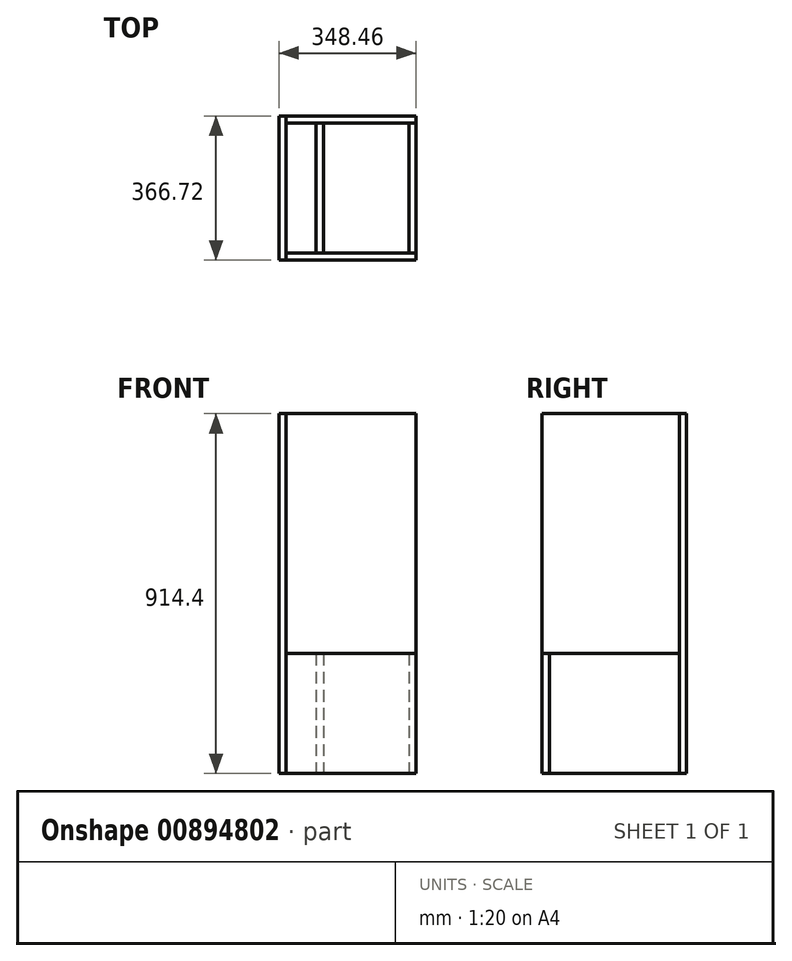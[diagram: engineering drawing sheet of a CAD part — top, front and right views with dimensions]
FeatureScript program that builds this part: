
annotation { "Feature Type Name" : "Feature", "Feature Type Description" : "" }
export const myFeature = defineFeature(function(context is Context, id is Id, definition is map)
    precondition{}
    {
        {
            assignVariable(context, id + "F0", {"name" : "PlyThick", "anyValue" : 23 / 812.8 * mm});
        }
        {
            assignVariable(context, id + "F1", {"name" : "HeightBack", "anyValue" : 914.4 * mm});
        }
        {
            assignVariable(context, id + "F2", {"name" : "HeightFront", "anyValue" : 304.8 * mm});
        }
        {
            var Q0;
            Q0=qCreatedBy(makeId("Top.planeOp"),FACE);
            var sketch = newSketch(context, id + "F3", { "sketchPlane" : qUnion([Q0])});
            skLineSegment(sketch, "E0.bottom", {"start": v(174.23, -183.36) * mm, "end": v(-174.23, -183.36) * mm});
            skLineSegment(sketch, "E0.top", {"start": v(174.23, 183.36) * mm, "end": v(-174.23, 183.36) * mm});
            skLineSegment(sketch, "E0.left", {"start": v(174.23, -183.36) * mm, "end": v(174.23, 183.36) * mm});
            skLineSegment(sketch, "E0.right", {"start": v(-174.23, -183.36) * mm, "end": v(-174.23, 183.36) * mm});
            skPoint(sketch, "E0.middle", {"position": v(0, 0) * mm});
            skLineSegment(sketch, "E1", {"start": v(-155.97, -183.36) * mm, "end": v(-155.97, 183.36) * mm});
            skLineSegment(sketch, "E2", {"start": v(-155.97, 165.1) * mm, "end": v(174.23, 165.1) * mm});
            skLineSegment(sketch, "E3", {"start": v(155.97, 165.1) * mm, "end": v(155.97, -165.1) * mm});
            skLineSegment(sketch, "E4", {"start": v(174.23, -165.1) * mm, "end": v(-155.97, -165.1) * mm});
            skLineSegment(sketch, "E5", {"start": v(-79.77, 165.1) * mm, "end": v(-79.77, -165.1) * mm, "construction": true});
            skLineSegment(sketch, "E6", {"start": v(-61.52, -165.1) * mm, "end": v(-61.52, 165.1) * mm, "construction": true});
            skSolve(sketch);
        }
        {
            var Q0;
            Q0=qCreatedBy(makeId("Top.planeOp"),FACE);
            var sketch = newSketch(context, id + "F4", { "sketchPlane" : qUnion([Q0])});
            skLineSegment(sketch, "E7.0.0", {"start": v(-155.97, -165.1) * mm, "end": v(155.97, -165.1) * mm});
            skLineSegment(sketch, "E7.0.1", {"start": v(155.97, -165.1) * mm, "end": v(155.97, 165.1) * mm});
            skLineSegment(sketch, "E7.0.2", {"start": v(155.97, 165.1) * mm, "end": v(-155.97, 165.1) * mm});
            skLineSegment(sketch, "E7.0.3", {"start": v(-155.97, 165.1) * mm, "end": v(-155.97, -165.1) * mm});
            skSolve(sketch);
        }
        {
            var Q0;
            Q0 = qSketchRegion(id + "F4", true);
            extrude(context, id + "F5", {"entities" : qUnion([Q0]), "depth" : getVariable(context, 'PlyThick'), "offsetDistance" : 25.4 * mm});
        }
        {
            var Q0;
            {var subQ4=sQuery(id+"F3.wireOp",EDGE,"E0.right");Q0=makeQuery(id+"F3.imprint","IMPRINT",FACE,{"disambiguationData":[TD([[makeQuery(id+"F3.imprint","IMPRINT",EDGE,{"derivedFrom":subQ4}),-1.0]])]});}
            extrude(context, id + "F6", {"entities" : qUnion([Q0]), "depth" : getVariable(context, 'HeightBack'), "offsetDistance" : 25.4 * mm});
        }
        {
            var Q0;
            {var subQ1=sQuery(id+"F3.wireOp",EDGE,"E0.top");var subQ6=sQuery(id+"F3.wireOp",EDGE,"E0.left");var subQ7=makeQuery(id+"F3.imprint","INTERSECT",VERTEX,{"derivedFrom":[subQ1,subQ6]});Q0=makeQuery(id+"F3.imprint","IMPRINT",FACE,{"disambiguationData":[TD([[makeQuery(id+"F3.imprint","IMPRINT",EDGE,{"disambiguationData":[TD([[subQ7,-1.0]])],"derivedFrom":subQ1}),1.0]])]});}
            extrude(context, id + "F7", {"entities" : qUnion([Q0]), "depth" : getVariable(context, 'HeightBack'), "offsetDistance" : 25.4 * mm});
        }
        {
            var Q0;
            {var subQ5=sQuery(id+"F3.wireOp",EDGE,"E4");Q0=makeQuery(id+"F3.imprint","IMPRINT",FACE,{"disambiguationData":[TD([[makeQuery(id+"F3.imprint","IMPRINT",EDGE,{"derivedFrom":subQ5}),1.0]])]});}
            extrude(context, id + "F8", {"entities" : qUnion([Q0]), "depth" : getVariable(context, 'HeightFront'), "offsetDistance" : 25.4 * mm});
        }
        {
            var Q0;
            {var subQ5=sQuery(id+"F3.wireOp",EDGE,"E3");Q0=makeQuery(id+"F3.imprint","IMPRINT",FACE,{"disambiguationData":[TD([[makeQuery(id+"F3.imprint","IMPRINT",EDGE,{"derivedFrom":subQ5}),1.0]])]});}
            extrude(context, id + "F9", {"entities" : qUnion([Q0]), "depth" : getVariable(context, 'HeightFront'), "offsetDistance" : 25.4 * mm});
        }
        {
            var Q0;
            Q0=makeQuery(id+"F5.opExtrude","CAP_FACE",FACE,{"disambiguationData":[OSD([sQuery(id+"F4.wireOp",EDGE,"E7.0.0"),sQuery(id+"F4.wireOp",EDGE,"E7.0.1"),sQuery(id+"F4.wireOp",EDGE,"E7.0.2"),sQuery(id+"F4.wireOp",EDGE,"E7.0.3")])],"isStart":false});
            var sketch = newSketch(context, id + "F10", { "sketchPlane" : qUnion([Q0])});
            skLineSegment(sketch, "E8.0", {"start": v(-79.77, 165.1) * mm, "end": v(-79.77, -165.1) * mm});
            skLineSegment(sketch, "E8.1", {"start": v(-61.52, -165.1) * mm, "end": v(-61.52, 165.1) * mm});
            skLineSegment(sketch, "E9", {"start": v(-61.52, 165.1) * mm, "end": v(-79.77, 165.1) * mm});
            skLineSegment(sketch, "E10", {"start": v(-79.77, -165.1) * mm, "end": v(-61.52, -165.1) * mm});
            skSolve(sketch);
        }
        {
            var Q0;
            Q0 = qSketchRegion(id + "F10", true);
            var Q1;
            Q1=makeQuery(id+"F8.opExtrude","CAP_FACE",FACE,{"disambiguationData":[OSD([sQuery(id+"F3.wireOp",EDGE,"E0.bottom"),sQuery(id+"F3.wireOp",EDGE,"E1"),sQuery(id+"F3.wireOp",EDGE,"E3"),sQuery(id+"F3.wireOp",EDGE,"E4")])],"isStart":false});
            extrude(context, id + "F11", {"entities" : qUnion([Q0]), "endBound" : BoundingType.UP_TO_SURFACE, "depth" : 25.4 * mm, "endBoundEntityFace" : qUnion([Q1]), "offsetDistance" : 25.4 * mm});
        }
    });
